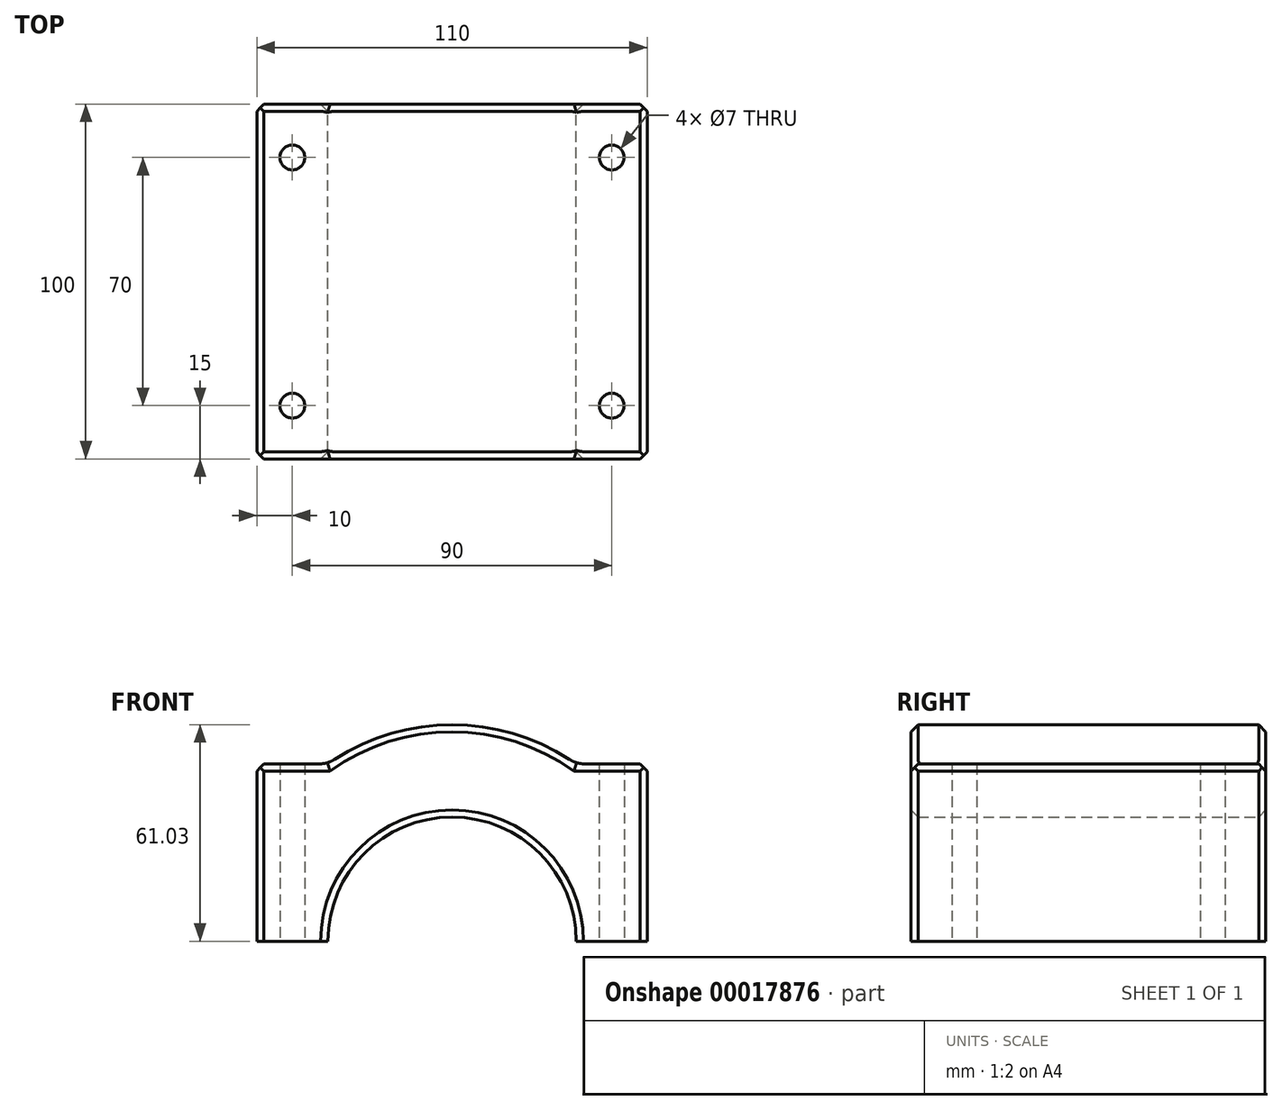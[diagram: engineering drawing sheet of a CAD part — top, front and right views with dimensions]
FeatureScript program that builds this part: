
annotation { "Feature Type Name" : "Feature", "Feature Type Description" : "" }
export const myFeature = defineFeature(function(context is Context, id is Id, definition is map)
    precondition{}
    {
        {
            var Q0;
            Q0=qCreatedBy(makeId("Front.planeOp"),FACE);
            var sketch = newSketch(context, id + "F0", { "sketchPlane" : qUnion([Q0])});
            skLineSegment(sketch, "E0", {"start": v(-110, 0) * mm, "end": v(-90, 0) * mm});
            skLineSegment(sketch, "E1", {"start": v(0, 0) * mm, "end": v(-20, 0) * mm});
            skArc(sketch, "E2", {"start": v(-20, 0) * mm, "mid": v(-55, 35) * mm, "end": v(-90, 0) * mm});
            skLineSegment(sketch, "E3", {"start": v(-110, 50) * mm, "end": v(-90, 50) * mm});
            skLineSegment(sketch, "E4", {"start": v(-20, 50) * mm, "end": v(0, 50) * mm});
            skArc(sketch, "E5", {"start": v(-20, 50) * mm, "mid": v(-55, 61.03) * mm, "end": v(-90, 50) * mm});
            skLineSegment(sketch, "E6", {"start": v(-110, 50) * mm, "end": v(-110, 0) * mm});
            skLineSegment(sketch, "E7", {"start": v(0, 50) * mm, "end": v(0, 0) * mm});
            skSolve(sketch);
        }
        {
            var Q0;
            Q0 = qSketchRegion(id + "F0", true);
            extrude(context, id + "F1", {"entities" : qUnion([Q0]), "depth" : 100 * mm});
        }
        {
            var Q0;
            Q0=makeQuery(id+"F1.opExtrude","SWEPT_FACE",FACE,{"disambiguationData":[OSD([sQuery(id+"F0.wireOp",EDGE,"E3")])]});
            var sketch = newSketch(context, id + "F2", { "sketchPlane" : qUnion([Q0])});
            skLineSegment(sketch, "E8", {"start": v(-100, 0) * mm, "end": v(-100, -100) * mm});
            skLineSegment(sketch, "E9", {"start": v(-100, -15) * mm, "end": v(-122.98, -15) * mm});
            skLineSegment(sketch, "E10", {"start": v(-100, -85) * mm, "end": v(-126.44, -85) * mm});
            skSolve(sketch);
        }
        {
            var Q0;
            Q0=sQuery(id+"F2.wireOp",VERTEX,"E9.start");
            var Q1;
            Q1=sQuery(id+"F2.wireOp",VERTEX,"E10.start");
            var Q2;
            Q2=makeQuery(id+"F1.opExtrude","SWEPT_BODY",BODY,{"disambiguationData":[OSD([sQuery(id+"F0.wireOp",EDGE,"E0"),sQuery(id+"F0.wireOp",EDGE,"E1"),sQuery(id+"F0.wireOp",EDGE,"E2"),sQuery(id+"F0.wireOp",EDGE,"E3"),sQuery(id+"F0.wireOp",EDGE,"E4"),sQuery(id+"F0.wireOp",EDGE,"E5"),sQuery(id+"F0.wireOp",EDGE,"E6"),sQuery(id+"F0.wireOp",EDGE,"E7")])]});
            hole(context, id + "F3", {"style" : HoleStyle.SIMPLE, "holeDiameter" : 7 * mm, "endStyle" : HoleEndStyle.THROUGH, "locations" : qUnion([Q0, Q1]), "scope" : qUnion([Q2])});
        }
        {
            var Q0;
            Q0=makeQuery(id+"F1.opExtrude","SWEPT_FACE",FACE,{"disambiguationData":[OSD([sQuery(id+"F0.wireOp",EDGE,"E4")])]});
            var sketch = newSketch(context, id + "F4", { "sketchPlane" : qUnion([Q0])});
            skLineSegment(sketch, "E11", {"start": v(-10, 0) * mm, "end": v(-10, -100) * mm});
            skLineSegment(sketch, "E12", {"start": v(-10, -15) * mm, "end": v(9.46, -15) * mm});
            skLineSegment(sketch, "E13", {"start": v(-10, -85) * mm, "end": v(10.95, -85) * mm});
            skSolve(sketch);
        }
        {
            var Q0;
            Q0=sQuery(id+"F4.wireOp",VERTEX,"E12.start");
            var Q1;
            Q1=sQuery(id+"F4.wireOp",VERTEX,"E13.start");
            var Q2;
            Q2=makeQuery(id+"F1.opExtrude","SWEPT_BODY",BODY,{"disambiguationData":[OSD([sQuery(id+"F0.wireOp",EDGE,"E0"),sQuery(id+"F0.wireOp",EDGE,"E1"),sQuery(id+"F0.wireOp",EDGE,"E2"),sQuery(id+"F0.wireOp",EDGE,"E3"),sQuery(id+"F0.wireOp",EDGE,"E4"),sQuery(id+"F0.wireOp",EDGE,"E5"),sQuery(id+"F0.wireOp",EDGE,"E6"),sQuery(id+"F0.wireOp",EDGE,"E7")])]});
            hole(context, id + "F5", {"style" : HoleStyle.SIMPLE, "holeDiameter" : 7 * mm, "endStyle" : HoleEndStyle.THROUGH, "locations" : qUnion([Q0, Q1]), "scope" : qUnion([Q2])});
        }
        {
            var Q0;
            Q0=makeQuery(id+"F1.opExtrude","CAP_EDGE",EDGE,{"disambiguationData":[OSD([sQuery(id+"F0.wireOp",EDGE,"E5")])],"isStart":false});
            var Q1;
            Q1=makeQuery(id+"F1.opExtrude","CAP_EDGE",EDGE,{"disambiguationData":[OSD([sQuery(id+"F0.wireOp",EDGE,"E4")])],"isStart":false});
            var Q2;
            Q2=makeQuery(id+"F1.opExtrude","SWEPT_EDGE",EDGE,{"disambiguationData":[OSD([sQuery(id+"F0.wireOp",EDGE,"E4"),sQuery(id+"F0.wireOp",EDGE,"E7")])]});
            var Q3;
            Q3=makeQuery(id+"F1.opExtrude","CAP_EDGE",EDGE,{"disambiguationData":[OSD([sQuery(id+"F0.wireOp",EDGE,"E4")])],"isStart":true});
            var Q4;
            Q4=makeQuery(id+"F1.opExtrude","CAP_EDGE",EDGE,{"disambiguationData":[OSD([sQuery(id+"F0.wireOp",EDGE,"E5")])],"isStart":true});
            var Q5;
            Q5=makeQuery(id+"F1.opExtrude","CAP_EDGE",EDGE,{"disambiguationData":[OSD([sQuery(id+"F0.wireOp",EDGE,"E3")])],"isStart":true});
            var Q6;
            Q6=makeQuery(id+"F1.opExtrude","SWEPT_EDGE",EDGE,{"disambiguationData":[OSD([sQuery(id+"F0.wireOp",EDGE,"E3"),sQuery(id+"F0.wireOp",EDGE,"E6")])]});
            var Q7;
            Q7=makeQuery(id+"F1.opExtrude","CAP_EDGE",EDGE,{"disambiguationData":[OSD([sQuery(id+"F0.wireOp",EDGE,"E3")])],"isStart":false});
            chamfer(context, id + "F6", {"entities" : qUnion([Q0, Q1, Q2, Q3, Q4, Q5, Q6, Q7]), "width" : 2 * mm, "tangentPropagation" : true});
        }
        {
            var Q0;
            Q0=makeQuery(id+"F1.opExtrude","SWEPT_EDGE",EDGE,{"disambiguationData":[OSD([sQuery(id+"F0.wireOp",EDGE,"E3"),sQuery(id+"F0.wireOp",EDGE,"E5")])]});
            var Q1;
            Q1=makeQuery(id+"F1.opExtrude","SWEPT_EDGE",EDGE,{"disambiguationData":[OSD([sQuery(id+"F0.wireOp",EDGE,"E4"),sQuery(id+"F0.wireOp",EDGE,"E5")])]});
            fillet(context, id + "F7", {"entities" : qUnion([Q0, Q1]), "radius" : 8 * mm, "tangentPropagation" : true, "allowEdgeOverflow" : false});
        }
        {
            var Q0;
            Q0=makeQuery(id+"F1.opExtrude","CAP_EDGE",EDGE,{"disambiguationData":[OSD([sQuery(id+"F0.wireOp",EDGE,"E7")])],"isStart":true});
            var Q1;
            Q1=makeQuery(id+"F1.opExtrude","CAP_EDGE",EDGE,{"disambiguationData":[OSD([sQuery(id+"F0.wireOp",EDGE,"E6")])],"isStart":true});
            var Q2;
            Q2=makeQuery(id+"F1.opExtrude","CAP_EDGE",EDGE,{"disambiguationData":[OSD([sQuery(id+"F0.wireOp",EDGE,"E7")])],"isStart":false});
            var Q3;
            Q3=makeQuery(id+"F1.opExtrude","CAP_EDGE",EDGE,{"disambiguationData":[OSD([sQuery(id+"F0.wireOp",EDGE,"E6")])],"isStart":false});
            chamfer(context, id + "F8", {"entities" : qUnion([Q0, Q1, Q2, Q3]), "width" : 2 * mm, "tangentPropagation" : true});
        }
        {
            var Q0;
            Q0=makeQuery(id+"F1.opExtrude","CAP_EDGE",EDGE,{"disambiguationData":[OSD([sQuery(id+"F0.wireOp",EDGE,"E2")])],"isStart":false});
            var Q1;
            Q1=makeQuery(id+"F1.opExtrude","CAP_EDGE",EDGE,{"disambiguationData":[OSD([sQuery(id+"F0.wireOp",EDGE,"E2")])],"isStart":true});
            chamfer(context, id + "F9", {"entities" : qUnion([Q0, Q1]), "width" : 2 * mm, "tangentPropagation" : true});
        }
    });
